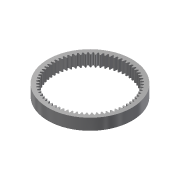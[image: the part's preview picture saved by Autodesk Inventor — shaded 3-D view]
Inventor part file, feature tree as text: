
AUTODESK INVENTOR PART (.ipt)
format: ipt  version: 2018 (Build 220112000, 112)  size: 427,520 bytes
history: native  units: mm (DEFAULTED — no unit token found)
features: plane x3, other x3, sketch x2, extrude x1
ambient origin geometry x8: Origin, YZ Plane, XZ Plane, XY Plane, X Axis, Y Axis, Z Axis, Center Point
bodies: Solid1 (feature_tree)
feature tree (9):
  extrude  "Extrusion1"  Depth=15.0mm TaperAngle=0.0deg
  plane  "Work Plane2"
  plane  "Work Plane8"
  plane  "Work Plane9"
  other  "正齒輪"
  sketch  "Sketch1"  dims[d0=111.375mm d1=15.0mm d2=0.0mm]
  sketch  "Sketch2"  dims[d3=97.5mm d4=10.0mm d5=0.0mm d16=6.0mm d17=0.0mm d34=0.483322mm d39=0.0mm d45=0.0mm d47=6.0mm d50=0.0mm d51=0.0mm d52=6.0mm]
  other  "Srf1"
  other  "節圓直徑"
